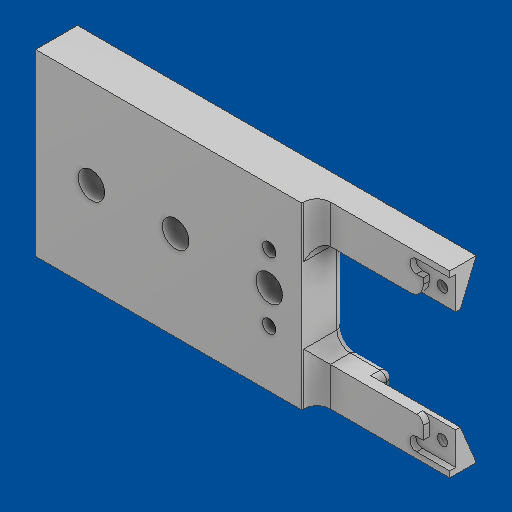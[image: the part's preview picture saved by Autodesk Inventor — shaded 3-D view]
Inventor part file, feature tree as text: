
AUTODESK INVENTOR PART (.ipt)
format: ipt  version: 2025 (Build 290162000, 162)  size: 225,792 bytes
history: native  units: in
note: dims shown in document units (in); Inventor stores cm internally (conversion verified against a paired STEP export)
features: fillet x3, direct_edit x3, other x3, move_body x2, hole x1, sketch x1
ambient origin geometry x8: Origin, YZ Plane, XZ Plane, XY Plane, X Axis, Y Axis, Z Axis, Center Point
bodies: Solid1 (feature_tree), Body1 (feature_tree)
feature tree (13):
  fillet  "Fillet1"  Radius=0.0394in
  direct_edit  "Direct Edit1"
  fillet  "Fillet2"  [1 undecoded]
  fillet  "Fillet3"  Radius=0.0394in
  direct_edit  "Direct Edit2"
  direct_edit  "Direct Edit3"
  hole  "Hole1"  [1 undecoded]
  sketch  "Sketch1"  dims[d1=0.0in d2=0.0in d3=-0.002in d4=0.0in d5=0.0in d6=-0.002in d7=0.0394in d8=0.0787in d9=-0.0079in d10=-0.0079in d11=0.0315in d12=0.0118in d13=0.0118in d14=0.0617in d15=0.1575in d16=0.1575in d17=0.0787in d18=90.0deg d19=0.248in d20=0.8108in]
  move_body  "Move1"
  move_body  "Move2"
  other  "Size1"
  other  "Size2"
  other  "Size3"
note: 2 required parameter values undecoded (feature->parameter linkage not recoverable at this tier; creation-order binding heuristic only, values carry confidence <= 0.55)
